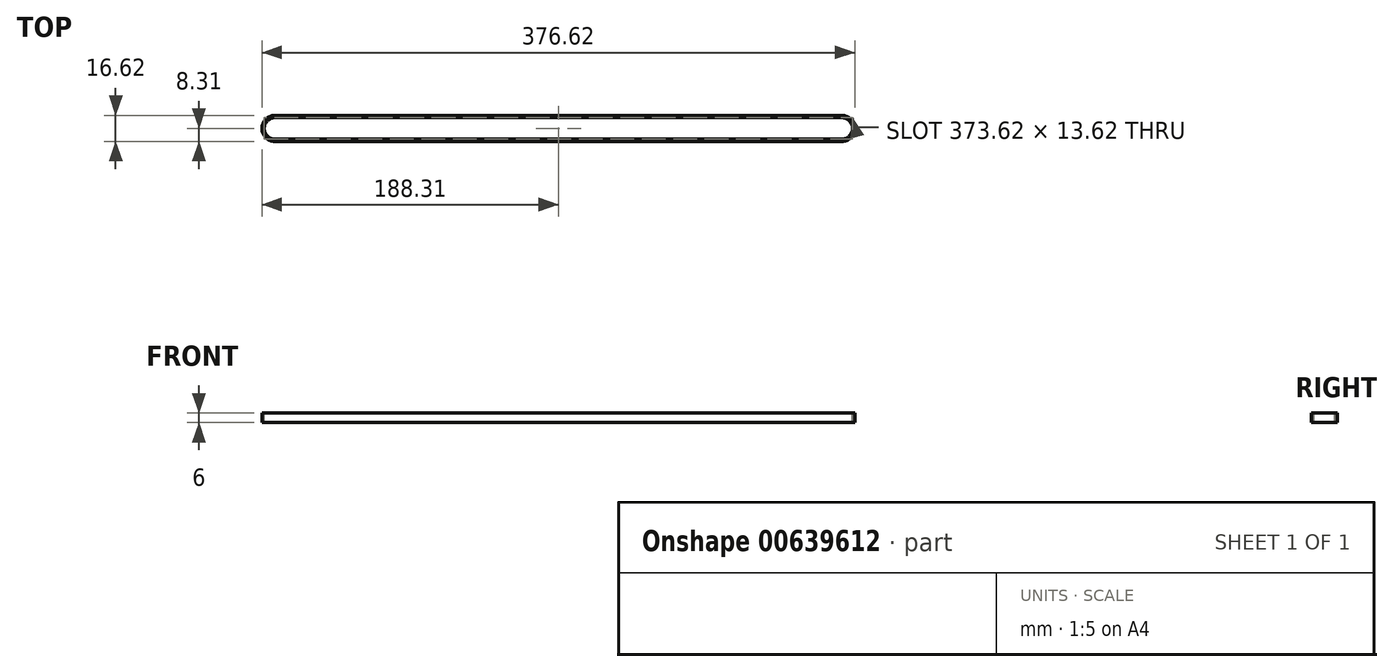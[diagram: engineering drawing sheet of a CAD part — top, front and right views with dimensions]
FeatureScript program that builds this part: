
annotation { "Feature Type Name" : "Feature", "Feature Type Description" : "" }
export const myFeature = defineFeature(function(context is Context, id is Id, definition is map)
    precondition{}
    {
        {
            var Q0;
            Q0=qCreatedBy(makeId("Top.planeOp"),FACE);
            var sketch = newSketch(context, id + "F0", { "sketchPlane" : qUnion([Q0])});
            skLineSegment(sketch, "E0", {"start": v(0, 7.56) * mm, "end": v(-180, 7.56) * mm});
            skArc(sketch, "E1", {"start": v(-180, 7.56) * mm, "mid": v(-185.35, 5.35) * mm, "end": v(-187.56, 0) * mm});
            skLineSegment(sketch, "E2.MirrorCS", {"start": v(0, -7.56) * mm, "end": v(-180, -7.56) * mm});
            skArc(sketch, "E3.MirrorCS", {"start": v(-180, -7.56) * mm, "mid": v(-185.35, -5.35) * mm, "end": v(-187.56, 0) * mm});
            skLineSegment(sketch, "E4.MirrorCS", {"start": v(0, 7.56) * mm, "end": v(180, 7.56) * mm});
            skArc(sketch, "E5.MirrorCS", {"start": v(180, 7.56) * mm, "mid": v(185.35, 5.35) * mm, "end": v(187.56, 0) * mm});
            skArc(sketch, "E6.MirrorCS", {"start": v(180, -7.56) * mm, "mid": v(185.35, -5.35) * mm, "end": v(187.56, 0) * mm});
            skLineSegment(sketch, "E7.MirrorCS", {"start": v(0, -7.56) * mm, "end": v(180, -7.56) * mm});
            skSolve(sketch);
        }
        {
            var Q0;
            Q0=qCreatedBy(makeId("Right.planeOp"),FACE);
            var sketch = newSketch(context, id + "F1", { "sketchPlane" : qUnion([Q0])});
            skLineSegment(sketch, "E8.bottom", {"start": v(-8.3, -3) * mm, "end": v(-6.8, -3) * mm});
            skLineSegment(sketch, "E8.top", {"start": v(-8.3, 3) * mm, "end": v(-6.8, 3) * mm});
            skLineSegment(sketch, "E8.left", {"start": v(-8.3, -3) * mm, "end": v(-8.3, 3) * mm});
            skLineSegment(sketch, "E8.right", {"start": v(-6.8, -3) * mm, "end": v(-6.8, 3) * mm});
            skPoint(sketch, "E8.middle", {"position": v(-7.56, 0) * mm});
            skSolve(sketch);
        }
        {
            var Q0;
            Q0=makeQuery(id+"F1.imprint","IMPRINT",FACE,{"disambiguationData":[TD([[makeQuery(id+"F1.imprint","IMPRINT",EDGE,{"derivedFrom":sQuery(id+"F1.wireOp",EDGE,"E8.bottom")}),1.0]])]});
            var Q1;
            Q1=sQuery(id+"F0.wireOp",EDGE,"E2.MirrorCS");
            var Q2;
            Q2=sQuery(id+"F0.wireOp",EDGE,"E3.MirrorCS");
            var Q3;
            Q3=sQuery(id+"F0.wireOp",EDGE,"E1");
            var Q4;
            Q4=sQuery(id+"F0.wireOp",EDGE,"E0");
            var Q5;
            Q5=sQuery(id+"F0.wireOp",EDGE,"E4.MirrorCS");
            var Q6;
            Q6=sQuery(id+"F0.wireOp",EDGE,"E5.MirrorCS");
            var Q7;
            Q7=sQuery(id+"F0.wireOp",EDGE,"E6.MirrorCS");
            var Q8;
            Q8=sQuery(id+"F0.wireOp",EDGE,"E7.MirrorCS");
            sweep(context, id + "F2", {"profiles" : qUnion([Q0]), "path" : qUnion([Q1, Q2, Q3, Q4, Q5, Q6, Q7, Q8])});
        }
    });
